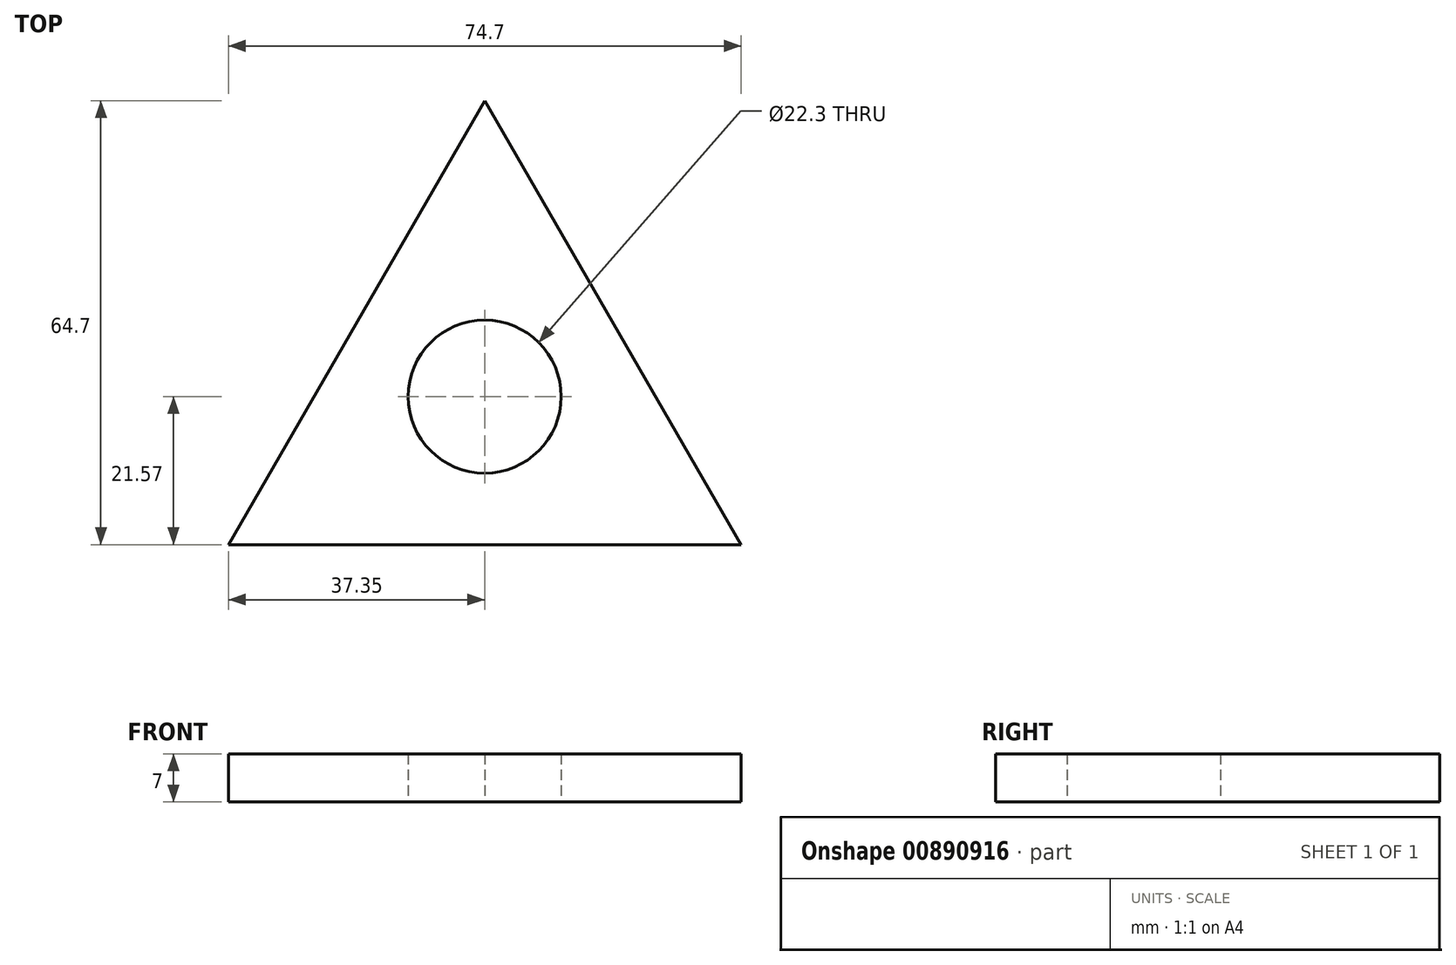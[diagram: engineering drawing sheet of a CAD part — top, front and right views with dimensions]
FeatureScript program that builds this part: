
annotation { "Feature Type Name" : "Feature", "Feature Type Description" : "" }
export const myFeature = defineFeature(function(context is Context, id is Id, definition is map)
    precondition{}
    {
        {
            var Q0;
            Q0=qCreatedBy(makeId("Top.planeOp"),FACE);
            var sketch = newSketch(context, id + "F0", { "sketchPlane" : qUnion([Q0])});
            skPoint(sketch, "E0.center", {"position": v(0, 0) * mm});
            skPoint(sketch, "E1.orphan", {"position": v(13.87, 0) * mm});
            skPoint(sketch, "E2.orphan", {"position": v(6.6, 11.43) * mm});
            skPoint(sketch, "E3.orphan", {"position": v(-6.93, 12) * mm});
            skPoint(sketch, "E4.orphan", {"position": v(-13.2, 0) * mm});
            skPoint(sketch, "E5.orphan", {"position": v(6.6, -11.43) * mm});
            skPoint(sketch, "E6.orphan", {"position": v(-6.93, -12) * mm});
            skPoint(sketch, "E7.orphan", {"position": v(0, 43.13) * mm});
            skPoint(sketch, "E8.orphan", {"position": v(37.35, -21.57) * mm});
            skPoint(sketch, "E9.orphan", {"position": v(-37.35, -21.57) * mm});
            skPoint(sketch, "E10.start.orphan", {"position": v(0, -11.15) * mm});
            skPoint(sketch, "E11.end.orphan", {"position": v(0, -17.28) * mm});
            skLineSegment(sketch, "E12", {"start": v(37.35, -21.57) * mm, "end": v(0, 43.13) * mm});
            skLineSegment(sketch, "E13", {"start": v(-37.35, -21.57) * mm, "end": v(0, 43.13) * mm});
            skLineSegment(sketch, "E14", {"start": v(-37.35, -21.57) * mm, "end": v(37.35, -21.57) * mm});
            skCircle(sketch, "E15", {"center": v(0, 0) * mm, "radius": 11.15 * mm});
            skSolve(sketch);
        }
        {
            var Q0;
            Q0=makeQuery(id+"F0.imprint","IMPRINT",FACE,{"disambiguationData":[TD([[makeQuery(id+"F0.imprint","IMPRINT",EDGE,{"derivedFrom":sQuery(id+"F0.wireOp",EDGE,"E12")}),1.0]])]});
            extrude(context, id + "F1", {"entities" : qUnion([Q0]), "depth" : 7 * mm, "offsetDistance" : 25 * mm});
        }
    });
